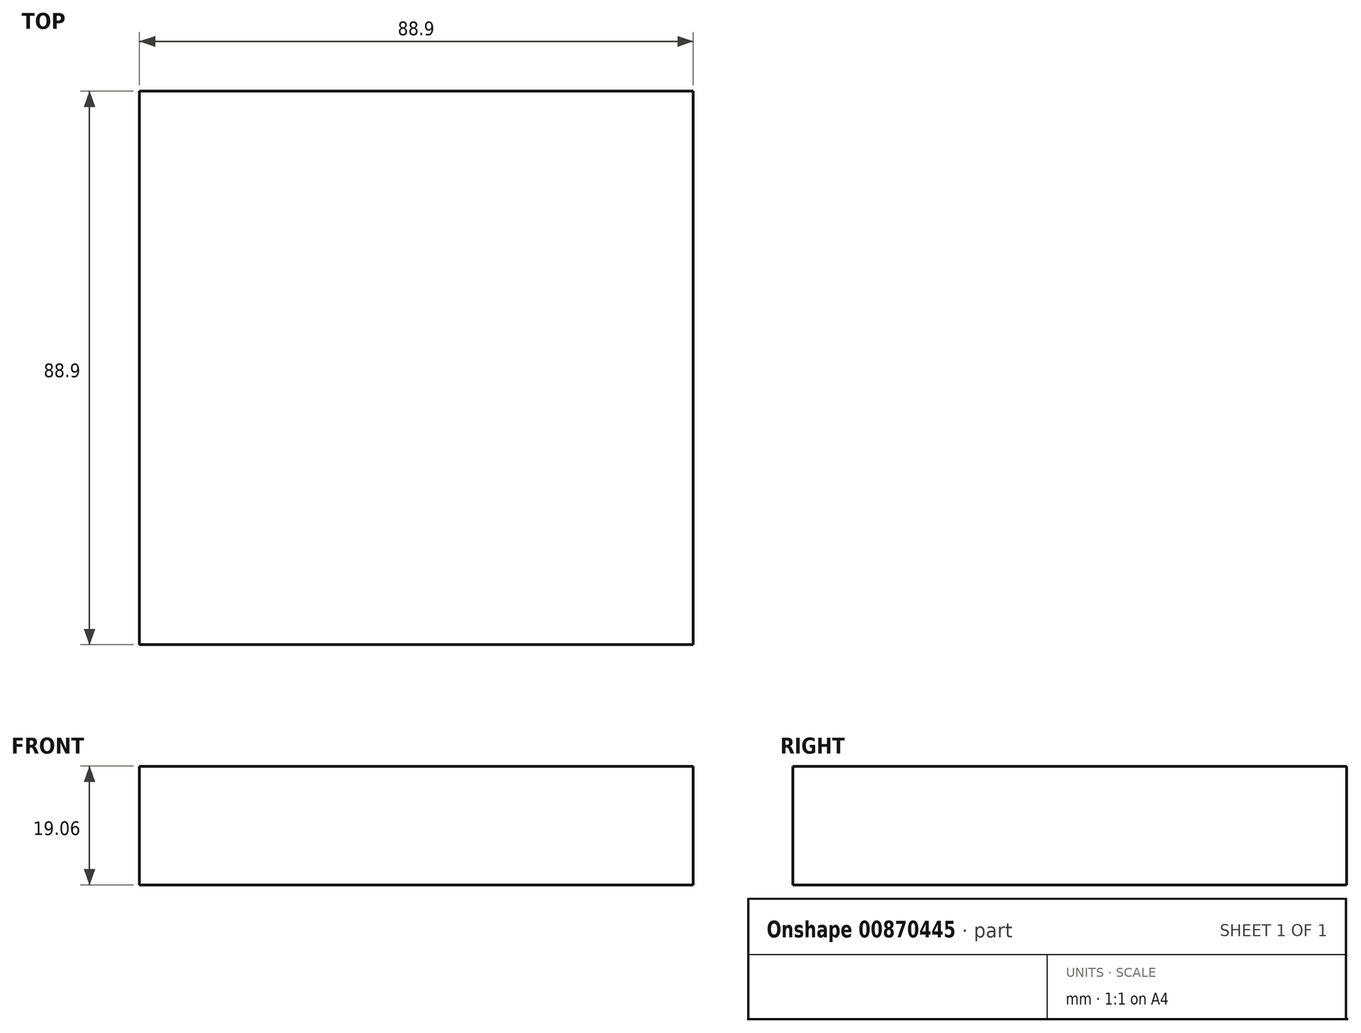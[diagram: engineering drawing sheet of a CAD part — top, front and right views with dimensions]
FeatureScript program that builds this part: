
annotation { "Feature Type Name" : "Feature", "Feature Type Description" : "" }
export const myFeature = defineFeature(function(context is Context, id is Id, definition is map)
    precondition{}
    {
        {
            var Q0;
            Q0=qCreatedBy(makeId("Right.planeOp"),FACE);
            var sketch = newSketch(context, id + "F0", { "sketchPlane" : qUnion([Q0])});
            skLineSegment(sketch, "E0.bottom", {"start": v(46.26, 9.53) * mm, "end": v(-42.64, 9.53) * mm});
            skLineSegment(sketch, "E0.top", {"start": v(46.26, -9.53) * mm, "end": v(-42.64, -9.53) * mm});
            skLineSegment(sketch, "E0.left", {"start": v(46.26, 9.53) * mm, "end": v(46.26, -9.52) * mm});
            skLineSegment(sketch, "E0.right", {"start": v(-42.64, 9.53) * mm, "end": v(-42.64, -9.52) * mm});
            skPoint(sketch, "E0.middle", {"position": v(1.8, 0) * mm});
            skSolve(sketch);
        }
        {
            var Q0;
            Q0=makeQuery(id+"F0.imprint","IMPRINT",FACE,{"disambiguationData":[TD([[makeQuery(id+"F0.imprint","IMPRINT",EDGE,{"derivedFrom":sQuery(id+"F0.wireOp",EDGE,"E0.bottom")}),1.0]])]});
            extrude(context, id + "F1", {"entities" : qUnion([Q0]), "depth" : 88.9 * mm, "offsetDistance" : 25.4 * mm});
        }
    });
